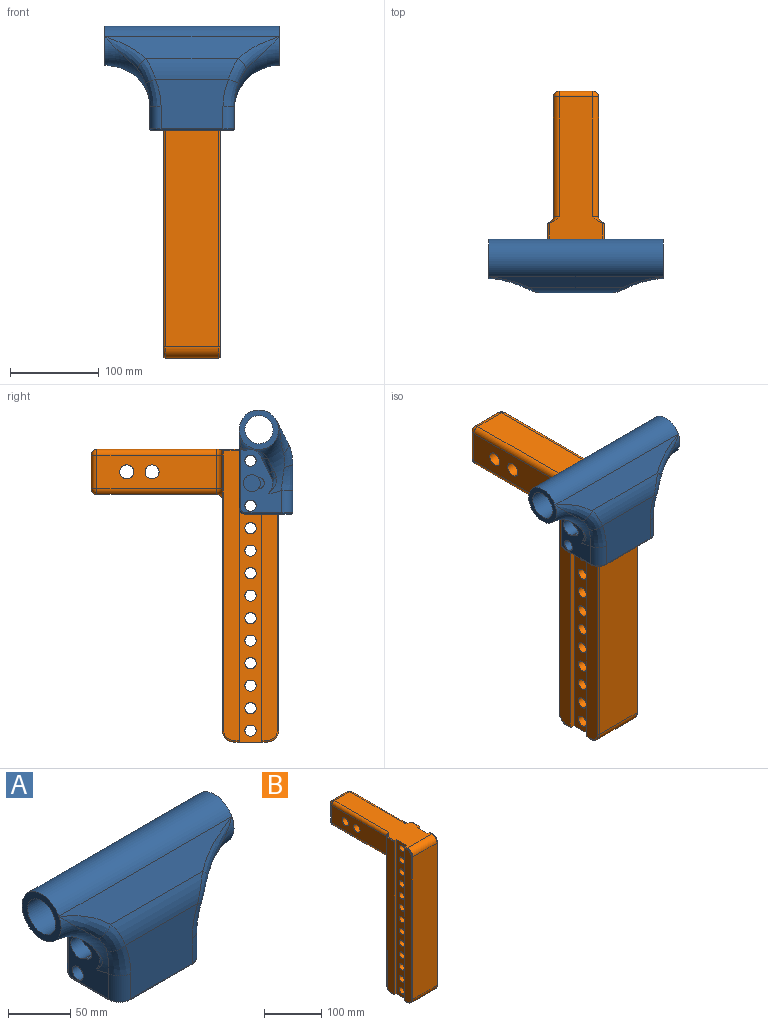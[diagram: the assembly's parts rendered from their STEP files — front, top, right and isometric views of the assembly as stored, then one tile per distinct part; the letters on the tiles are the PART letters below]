
ASSEMBLY  parts=2 mates=1
PART A: 63 faces, bbox 233.7x237x173 mm
  f0: torus R=73.03mm, axis (1,0,0), area 4002.1mm2, adj f4,f17,f21,f24,f25,f49,f53
  f1: torus R=73.03mm, axis (1,0,0), area 2216.2mm2, adj f3,f22,f26,f28,f40,f42,f43,f44
  f2: cylinder r=6.35mm len=22.23mm, axis (-1,0,0), area 886.7mm2, adj f3,f11
  f3: plane 73.33x46.87mm, normal (-1,0,0), area 1889.2mm2, adj f1,f2,f15,f27,f29,f30,f35,f36
  f4: plane 41.28x25.2mm, normal (1,0,0), area 772.4mm2, adj f0,f16,f23,f48,f56
  f5: plane 73.98x25.4mm, normal (-1,0,0), area 1617mm2, adj f6,f12,f14,f16,f17,f47,f54
  f6: plane 73.98x6.35mm, normal (0,-1,0), area 469.8mm2, adj f5,f7,f14,f54
  f7: plane 73.98x19.05mm, normal (-1,0,0), area 1409.3mm2, adj f6,f8,f14,f54
  f8: plane 73.98x63.5mm, normal (0,1,0), area 4697.6mm2, adj f7,f9,f14,f54
  f9: plane 73.98x19.05mm, normal (1,0,0), area 1409.3mm2, adj f8,f10,f14,f54
  f10: plane 73.98x6.35mm, normal (0,-1,0), area 469.8mm2, adj f9,f11,f14,f54
  f11: plane 73.98x25.4mm, normal (1,0,0), area 1617mm2, adj f2,f10,f12,f14,f15,f50,f54
  f12: plane 196.85x88.9mm, normal (0,1,0), area 6166.1mm2, adj f5,f11,f19,f39,f40,f47,f48,f49
  f13: plane 82.45x55.95mm, normal (0,-1,0), area 4037.3mm2, adj f23,f24,f27,f28,f52,f58
  f14: plane 92.08x52.39mm, normal (0,0,-1), area 2593.2mm2, adj f5,f6,f7,f8,f9,f10,f11,f47
  f15: cylinder r=6.35mm len=22.23mm, axis (-1,0,0), area 886.7mm2, adj f3,f11
  f16: cylinder r=6.35mm len=22.23mm, axis (-1,0,0), area 886.7mm2, adj f4,f5
  f17: cylinder r=6.35mm len=46.26mm, axis (-1,0,0), area 1531.9mm2, adj f0,f5
  f18: plane 196.85x24.64mm, normal (0,-0.89,0.46), area 3941.2mm2, adj f19,f25,f26,f52
  f19: cylinder r=22.23mm len=196.85mm, axis (-1,0,0), area 11661.9mm2, adj f12,f18,f21,f22
  f20: cylinder r=15.88mm len=196.85mm, axis (-1,0,0), area 19634.9mm2, adj f21,f22
  f21: plane 44.45x44.45mm, normal (1,0,0), area 760.1mm2, adj f0,f19,f20
  f22: plane 44.45x44.45mm, normal (-1,0,0), area 760.1mm2, adj f1,f19,f20
  f23: cylinder r=12.7mm len=25.2mm, axis (0,0,-1), area 502.7mm2, adj f4,f13,f24,f57
  f24: bspline ~41.57x18.73mm, area 531.9mm2, adj f0,f13,f23,f53
  f25: bspline ~50.89x41.31mm, area 342.9mm2, adj f0,f18,f53
  f26: bspline ~50.89x41.31mm, area 342.9mm2, adj f1,f18,f51
  f27: cylinder r=12.7mm len=25.2mm, axis (0,0,1), area 502.7mm2, adj f3,f13,f28,f59
  f28: bspline ~41.57x18.73mm, area 531.9mm2, adj f1,f13,f27,f51
  f29: plane 16.51x14.59mm, normal (0,0.9,-0.44), area 115mm2, adj f3,f30,f42,f43
  f30: cylinder r=12.7mm len=38.8mm, axis (-1,0,0), area 569.7mm2, adj f3,f29,f39,f42
  f31: plane 19.05x19.05mm, normal (-1,0,0), area 285mm2, adj f38
  f32: plane 12.66x10.02mm, normal (-1,0,0), area 88.8mm2, adj f33,f36,f37,f38
  f33: cylinder r=6.34mm len=12.66mm, axis (-1,0,0), area 146.9mm2, adj f32,f34,f36,f37
  f34: plane 12.66x9.01mm, normal (1,0,0), area 40mm2, adj f33,f35,f36,f37
  f35: cylinder r=6.35mm len=12.66mm, axis (-1,0,0), area 72.2mm2, adj f3,f34,f36,f37
  f36: plane 11.43x4mm, normal (0,0,1), area 34.3mm2, adj f3,f32,f33,f34,f35,f38
  f37: plane 11.43x4mm, normal (0,0,-1), area 34.3mm2, adj f3,f32,f33,f34,f35,f38
  f38: cylinder r=9.53mm len=19.05mm, axis (-1,0,0), area 981.8mm2, adj f3,f31,f32,f36,f37
  f39: cylinder r=6.35mm len=24.33mm, axis (-1,0,0), area 279.6mm2, adj f3,f12,f30,f41,f62
  f40: bspline ~32.45x24.68mm, area 67.8mm2, adj f1,f12,f41
  f41: sphere r=6.35mm, area 23mm2, adj f39,f40,f42
  f42: bspline ~30.22x27.96mm, area 246.9mm2, adj f1,f29,f30,f41,f43
  f43: bspline ~24.79x24.49mm, area 204.4mm2, adj f1,f29,f42,f44
  f44: bspline ~10.77x10.15mm, area 63.5mm2, adj f1,f3,f43,f45
  f45: bspline ~12.82x5.56mm, area 48.3mm2, adj f1,f3,f44,f46
  f46: bspline ~11.74x8.5mm, area 4.4mm2, adj f1,f3,f45
  f47: cylinder r=6.35mm len=20.64mm, axis (1,0,0), area 182.1mm2, adj f5,f12,f14,f55
  f48: cylinder r=6.35mm len=22.38mm, axis (0,0,1), area 199.5mm2, adj f4,f12,f49,f55
  f49: bspline ~77.47x57.15mm, area 385.1mm2, adj f0,f12,f48
  f50: cylinder r=6.35mm len=20.64mm, axis (-1,0,0), area 205.8mm2, adj f11,f12,f14,f61
  f51: bspline ~34.55x23.75mm, area 380.6mm2, adj f1,f26,f28,f52
  f52: cylinder r=50.8mm len=104.75mm, axis (-1,0,0), area 2263.1mm2, adj f13,f18,f51,f53
  f53: bspline ~36.36x24.87mm, area 380.6mm2, adj f0,f24,f25,f52
  f54: plane 63.5x44.45mm, normal (0,0,-1), area 2500mm2, adj f5,f6,f7,f8,f9,f10,f11,f12
  f55: bspline ~7.38x6.35mm, area 10.9mm2, adj f47,f48,f56
  f56: cylinder r=1.59mm len=41.28mm, axis (0,1,0), area 102.9mm2, adj f4,f14,f55,f57
  f57: torus R=11.11mm, axis (0,0,1), area 47.5mm2, adj f14,f23,f56,f58
  f58: cylinder r=1.59mm len=69.85mm, axis (1,0,0), area 174.2mm2, adj f13,f14,f57,f59
  f59: torus R=11.11mm, axis (0,0,1), area 47.5mm2, adj f14,f27,f58,f60
  f60: cylinder r=1.59mm len=41.28mm, axis (0,-1,0), area 102.9mm2, adj f3,f14,f59,f61
  f61: torus R=4.76mm, axis (1,0,0), area 22.6mm2, adj f3,f50,f60,f62
  f62: cylinder r=1.59mm len=71.94mm, axis (0,0,-1), area 174.1mm2, adj f3,f12,f39,f61
PART B: 83 faces, bbox 75.4x212.5x343.5 mm
  f0: plane 0.2x0.11mm, normal (0,1,0), area 0mm2, adj f3,f51,f67
  f1: plane 0.2x0.11mm, normal (0,1,0), area 0mm2, adj f3,f45,f76
  f2: plane 266.9x60.33mm, normal (0,1,0), area 15747.7mm2, adj f47,f48,f49,f54,f72,f80
  f3: plane 192.41x60.33mm, normal (0,0,1), area 8266mm2, adj f0,f1,f18,f19,f20,f21,f24,f26
  f4: plane 60.33x38.1mm, normal (0,0,-1), area 2056.4mm2, adj f18,f19,f20,f21,f24,f26,f54,f55
  f5: cylinder r=6.35mm len=50.8mm, axis (-1,0,0), area 2026.8mm2, adj f18,f19
  f6: cylinder r=6.35mm len=50.8mm, axis (-1,0,0), area 2026.8mm2, adj f18,f19
  f7: cylinder r=6.35mm len=50.8mm, axis (-1,0,0), area 2026.8mm2, adj f18,f19
  f8: cylinder r=6.35mm len=50.8mm, axis (-1,0,0), area 2026.8mm2, adj f18,f19
  f9: cylinder r=6.35mm len=50.8mm, axis (-1,0,0), area 2026.8mm2, adj f18,f19
  f10: cylinder r=6.35mm len=50.8mm, axis (-1,0,0), area 2026.8mm2, adj f18,f19
  f11: cylinder r=6.35mm len=50.8mm, axis (-1,0,0), area 2026.8mm2, adj f18,f19
  f12: cylinder r=6.35mm len=50.8mm, axis (-1,0,0), area 2026.8mm2, adj f18,f19
  f13: cylinder r=6.35mm len=50.8mm, axis (-1,0,0), area 2026.8mm2, adj f18,f19
  f14: cylinder r=6.35mm len=50.8mm, axis (-1,0,0), area 2026.8mm2, adj f18,f19
  f15: cylinder r=6.35mm len=50.8mm, axis (-1,0,0), area 2026.8mm2, adj f18,f19
  f16: cylinder r=6.35mm len=50.8mm, axis (-1,0,0), area 2026.8mm2, adj f18,f19
  f17: cylinder r=6.35mm len=50.8mm, axis (-1,0,0), area 2026.8mm2, adj f18,f19
  f18: plane 330.2x25.4mm, normal (1,0,0), area 6740.3mm2, adj f3,f4,f5,f6,f7,f8,f9,f10
  f19: plane 330.2x25.4mm, normal (-1,0,0), area 6740.3mm2, adj f3,f4,f5,f6,f7,f8,f9,f10
  f20: plane 330.2x6.35mm, normal (0,-1,0), area 2095.7mm2, adj f3,f4,f18,f22,f75,f82
  f21: plane 330.2x6.35mm, normal (0,-1,0), area 2095.7mm2, adj f3,f4,f19,f23,f68,f74
  f22: plane 327.03x17.62mm, normal (1,0,0), area 5691.3mm2, adj f20,f75,f77,f78,f79,f80,f81,f82
  f23: plane 327.03x17.62mm, normal (-1,0,0), area 5691.3mm2, adj f21,f68,f69,f70,f71,f72,f73,f74
  f24: plane 330.2x6.35mm, normal (0,1,0), area 2095.7mm2, adj f3,f4,f18,f27,f57,f61
  f25: plane 304.8x60.33mm, normal (0,-1,0), area 18387.1mm2, adj f55,f56,f59,f64
  f26: plane 330.2x6.35mm, normal (0,1,0), area 2095.7mm2, adj f3,f4,f19,f28,f62,f66
  f27: plane 327.03x17.46mm, normal (1,0,0), area 5657.7mm2, adj f24,f57,f58,f59,f60,f61
  f28: plane 327.03x17.46mm, normal (-1,0,0), area 5657.7mm2, adj f26,f62,f63,f64,f65,f66
  f29: plane 135.26x38.1mm, normal (-1,0,0), area 4757.4mm2, adj f35,f41,f44,f50,f52,f53
  f30: plane 135.26x38.1mm, normal (1,0,0), area 4757.4mm2, adj f33,f37,f38,f46,f52,f53
  f31: plane 135.26x38.1mm, normal (0,0,-1), area 5153.2mm2, adj f33,f35,f36,f48
  f32: plane 38.1x38.1mm, normal (0,1,0), area 1451.6mm2, adj f36,f37,f41,f42
  f33: cylinder r=6.35mm len=135.26mm, axis (0,1,0), area 1349.1mm2, adj f30,f31,f34,f47
  f34: sphere r=6.35mm, area 40.3mm2, adj f33,f36,f37
  f35: cylinder r=6.35mm len=135.26mm, axis (0,-1,0), area 1349.1mm2, adj f29,f31,f39,f49
  f36: cylinder r=6.35mm len=38.1mm, axis (1,0,0), area 380mm2, adj f31,f32,f34,f39
  f37: cylinder r=6.35mm len=38.1mm, axis (0,0,1), area 380mm2, adj f30,f32,f34,f40
  f38: cylinder r=6.35mm len=135.26mm, axis (0,1,0), area 1349.1mm2, adj f3,f30,f40,f45
  f39: sphere r=6.35mm, area 40.3mm2, adj f35,f36,f41
  f40: sphere r=6.35mm, area 40.3mm2, adj f37,f38,f42
  f41: cylinder r=6.35mm len=38.1mm, axis (0,0,-1), area 380mm2, adj f29,f32,f39,f43
  f42: cylinder r=6.35mm len=38.1mm, axis (-1,0,0), area 380mm2, adj f3,f32,f40,f43
  f43: sphere r=6.35mm, area 86.4mm2, adj f41,f42,f44
  f44: cylinder r=6.35mm len=135.26mm, axis (0,-1,0), area 1349.1mm2, adj f3,f29,f43,f51
  f45: torus R=12.7mm, axis (0,1,0), area 70.4mm2, adj f1,f3,f38,f46,f77
  f46: cylinder r=6.35mm len=38.1mm, axis (0,0,-1), area 331.3mm2, adj f30,f45,f47,f78
  f47: torus R=12.7mm, axis (0,1,0), area 131.7mm2, adj f2,f33,f46,f48,f79
  f48: cylinder r=6.35mm len=38.1mm, axis (-1,0,0), area 380mm2, adj f2,f31,f47,f49
  f49: torus R=12.7mm, axis (0,1,0), area 131.7mm2, adj f2,f35,f48,f50,f71
  f50: cylinder r=6.35mm len=38.1mm, axis (0,0,1), area 331.3mm2, adj f29,f49,f51,f70
  f51: torus R=12.7mm, axis (0,1,0), area 70.4mm2, adj f0,f3,f44,f50,f69
  f52: cylinder r=7.94mm len=50.8mm, axis (-1,0,0), area 2533.5mm2, adj f29,f30
  f53: cylinder r=7.94mm len=50.8mm, axis (-1,0,0), area 2533.5mm2, adj f29,f30
  f54: cylinder r=12.7mm len=60.33mm, axis (1,0,0), area 1203.4mm2, adj f2,f4,f73,f81
  f55: cylinder r=12.7mm len=60.33mm, axis (-1,0,0), area 1203.4mm2, adj f4,f25,f58,f63
  f56: cylinder r=12.7mm len=60.33mm, axis (1,0,0), area 1203.4mm2, adj f3,f25,f60,f65
  f57: cylinder r=1.59mm len=6.35mm, axis (0,-1,0), area 15.8mm2, adj f4,f24,f27,f58
  f58: torus R=11.11mm, axis (1,0,0), area 47.5mm2, adj f27,f55,f57,f59
  f59: cylinder r=1.59mm len=304.8mm, axis (0,0,1), area 760.1mm2, adj f25,f27,f58,f60
  f60: torus R=11.11mm, axis (1,0,0), area 47.5mm2, adj f27,f56,f59,f61
  f61: cylinder r=1.59mm len=6.35mm, axis (0,1,0), area 15.8mm2, adj f3,f24,f27,f60
  f62: cylinder r=1.59mm len=6.35mm, axis (0,1,0), area 15.8mm2, adj f4,f26,f28,f63
  f63: torus R=11.11mm, axis (1,0,0), area 47.5mm2, adj f28,f55,f62,f64
  f64: cylinder r=1.59mm len=304.8mm, axis (0,0,-1), area 760.1mm2, adj f25,f28,f63,f65
  f65: torus R=11.11mm, axis (1,0,0), area 47.5mm2, adj f28,f56,f64,f66
  f66: cylinder r=1.59mm len=6.35mm, axis (0,-1,0), area 15.8mm2, adj f3,f26,f28,f65
  f67: cylinder r=1.59mm len=0.77mm, axis (0,0,1), area 0.1mm2, adj f0,f68,f69
  f68: cylinder r=1.59mm len=19.05mm, axis (0,-1,0), area 45.9mm2, adj f3,f21,f23,f67,f69
  f69: bspline ~9.53x1.73mm, area 13mm2, adj f23,f51,f67,f68,f70
  f70: cylinder r=1.59mm len=38.1mm, axis (0,0,1), area 82.8mm2, adj f23,f50,f69,f71
  f71: bspline ~10.27x2.12mm, area 14.1mm2, adj f23,f49,f70,f72
  f72: cylinder r=1.59mm len=266.9mm, axis (0,0,1), area 665.6mm2, adj f2,f23,f71,f73
  f73: torus R=11.11mm, axis (1,0,0), area 47.5mm2, adj f23,f54,f72,f74
  f74: cylinder r=1.59mm len=6.35mm, axis (0,1,0), area 15.8mm2, adj f4,f21,f23,f73
  f75: cylinder r=1.59mm len=19.05mm, axis (0,1,0), area 45.9mm2, adj f3,f20,f22,f76,f77
  f76: cylinder r=1.59mm len=0.77mm, axis (0,0,-1), area 0.1mm2, adj f1,f75,f77
  f77: bspline ~8.01x1.73mm, area 13mm2, adj f22,f45,f75,f76,f78
  f78: cylinder r=1.59mm len=38.1mm, axis (0,0,-1), area 82.8mm2, adj f22,f46,f77,f79
  f79: bspline ~8.52x1.79mm, area 14.1mm2, adj f22,f47,f78,f80
  f80: cylinder r=1.59mm len=266.9mm, axis (0,0,-1), area 665.6mm2, adj f2,f22,f79,f81
  f81: torus R=11.11mm, axis (1,0,0), area 47.5mm2, adj f22,f54,f80,f82
  f82: cylinder r=1.59mm len=6.35mm, axis (0,-1,0), area 15.8mm2, adj f4,f20,f22,f81
PLACE A t=(0,0,92.08)mm
PLACE B at identity
MATE fastened A.f2 <-> B.f16  axis (1,0,0) through (-25.4,0,152.4)mm
